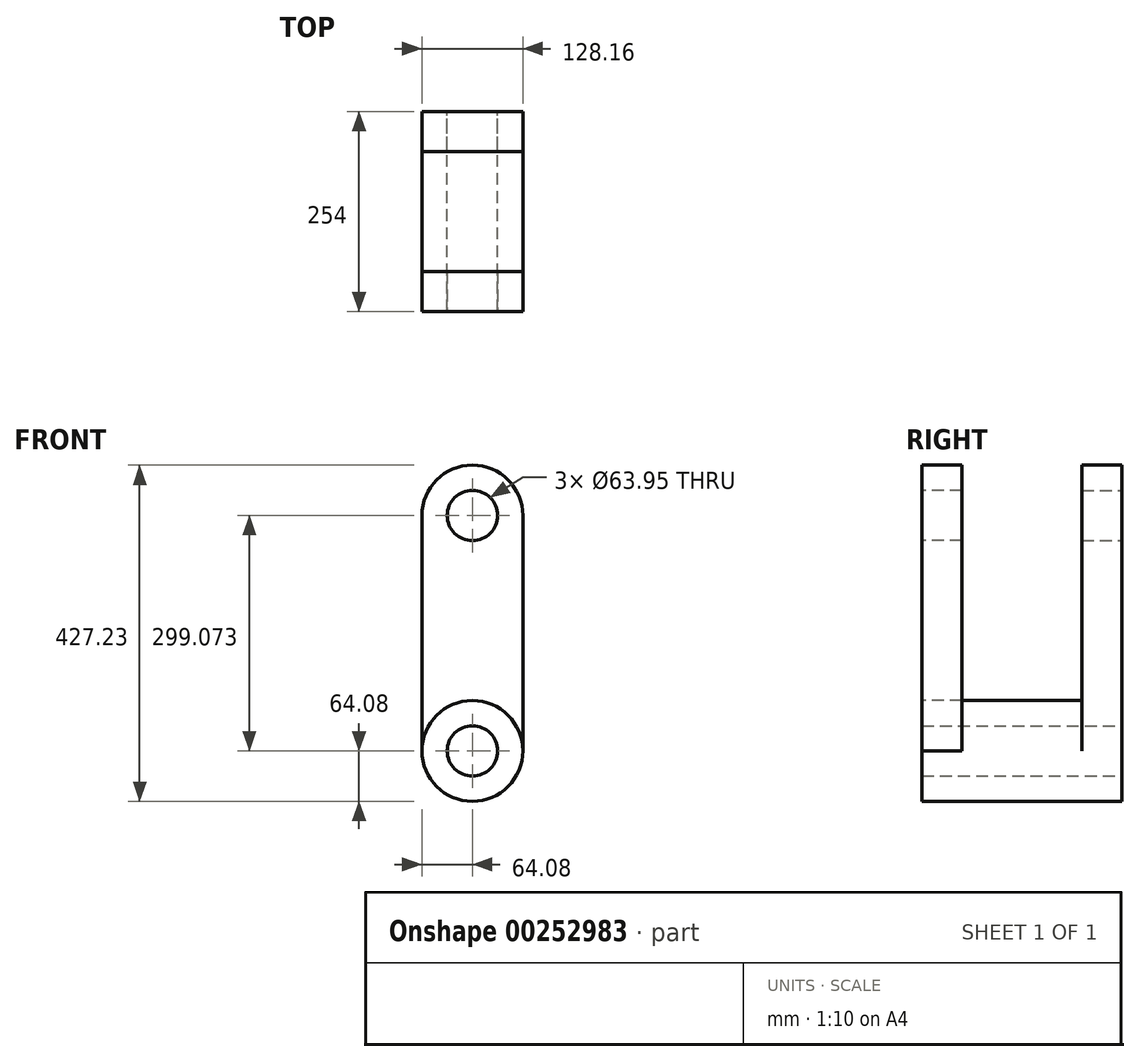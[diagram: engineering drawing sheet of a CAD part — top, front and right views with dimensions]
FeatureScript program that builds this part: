
annotation { "Feature Type Name" : "Feature", "Feature Type Description" : "" }
export const myFeature = defineFeature(function(context is Context, id is Id, definition is map)
    precondition{}
    {
        {
            var Q0;
            Q0=qCreatedBy(makeId("Front.planeOp"),FACE);
            var sketch = newSketch(context, id + "F0", { "sketchPlane" : qUnion([Q0])});
            skCircle(sketch, "E0", {"center": v(0, 0) * mm, "radius": 64.08 * mm});
            skCircle(sketch, "E1", {"center": v(0, 0) * mm, "radius": 31.97 * mm});
            skSolve(sketch);
        }
        {
            var Q0;
            Q0=makeQuery(id+"F0.imprint","IMPRINT",FACE,{"disambiguationData":[TD([[makeQuery(id+"F0.imprint","IMPRINT",EDGE,{"derivedFrom":sQuery(id+"F0.wireOp",EDGE,"E0")}),1.0]])]});
            extrude(context, id + "F1", {"entities" : qUnion([Q0]), "depth" : 254 * mm});
        }
        {
            var Q0;
            Q0=makeQuery(id+"F1.opExtrude","CAP_FACE",FACE,{"disambiguationData":[OSD([sQuery(id+"F0.wireOp",EDGE,"E0"),sQuery(id+"F0.wireOp",EDGE,"E1")])],"isStart":true});
            var sketch = newSketch(context, id + "F2", { "sketchPlane" : qUnion([Q0])});
            skCircle(sketch, "E2.0.0", {"center": v(0, 0) * mm, "radius": 64.08 * mm});
            skLineSegment(sketch, "E3.left", {"start": v(64.08, 0) * mm, "end": v(64.08, 0) * mm});
            skLineSegment(sketch, "E3.right", {"start": v(-64.08, 0) * mm, "end": v(-64.08, 0) * mm});
            skLineSegment(sketch, "E4.left", {"start": v(-64.08, 0) * mm, "end": v(-64.08, 299.07) * mm});
            skLineSegment(sketch, "E4.right", {"start": v(64.08, 0) * mm, "end": v(64.08, 299.07) * mm});
            skArc(sketch, "E5.MirrorC", {"start": v(-64.08, 299.07) * mm, "mid": v(0, 363.15) * mm, "end": v(64.08, 299.07) * mm});
            skCircle(sketch, "E6.0", {"center": v(0, 0) * mm, "radius": 31.97 * mm});
            skCircle(sketch, "E7.MirrorC", {"center": v(0, 299.07) * mm, "radius": 31.97 * mm});
            skPoint(sketch, "E8.end.orphan", {"position": v(-64.08, 149.54) * mm});
            skPoint(sketch, "E8.start.orphan", {"position": v(64.08, 149.54) * mm});
            skSolve(sketch);
        }
        {
            var Q0;
            Q0=qSketchRegion(id+"F2",true);
            extrude(context, id + "F3", {"entities" : qUnion([Q0]), "operationType" : NewBodyOperationType.ADD, "oppositeDirection" : true, "depth" : 50.8 * mm});
        }
        {
            var Q0;
            Q0=makeQuery(id+"F1.opExtrude","CAP_FACE",FACE,{"disambiguationData":[OSD([sQuery(id+"F0.wireOp",EDGE,"E0"),sQuery(id+"F0.wireOp",EDGE,"E1")])],"isStart":false});
            var sketch = newSketch(context, id + "F4", { "sketchPlane" : qUnion([Q0])});
            skCircle(sketch, "E9.0", {"center": v(0, 299.07) * mm, "radius": 31.97 * mm});
            skArc(sketch, "E10.0", {"start": v(64.08, 299.07) * mm, "mid": v(0, 363.15) * mm, "end": v(-64.08, 299.07) * mm});
            skLineSegment(sketch, "E11.0", {"start": v(64.08, 0) * mm, "end": v(64.08, 299.07) * mm});
            skLineSegment(sketch, "E12.0", {"start": v(-64.08, 0) * mm, "end": v(-64.08, 299.07) * mm});
            skCircle(sketch, "E13.0", {"center": v(0, 0) * mm, "radius": 64.08 * mm});
            skCircle(sketch, "E14.0", {"center": v(0, 0) * mm, "radius": 31.97 * mm});
            skSolve(sketch);
        }
        {
            var Q0;
            Q0=makeQuery(id+"F4.imprint","IMPRINT",FACE,{"disambiguationData":[TD([[makeQuery(id+"F4.imprint","IMPRINT",EDGE,{"derivedFrom":sQuery(id+"F4.wireOp",EDGE,"E9.0")}),-1.0]])]});
            extrude(context, id + "F5", {"entities" : qUnion([Q0]), "oppositeDirection" : true, "depth" : 50.8 * mm});
        }
    });
